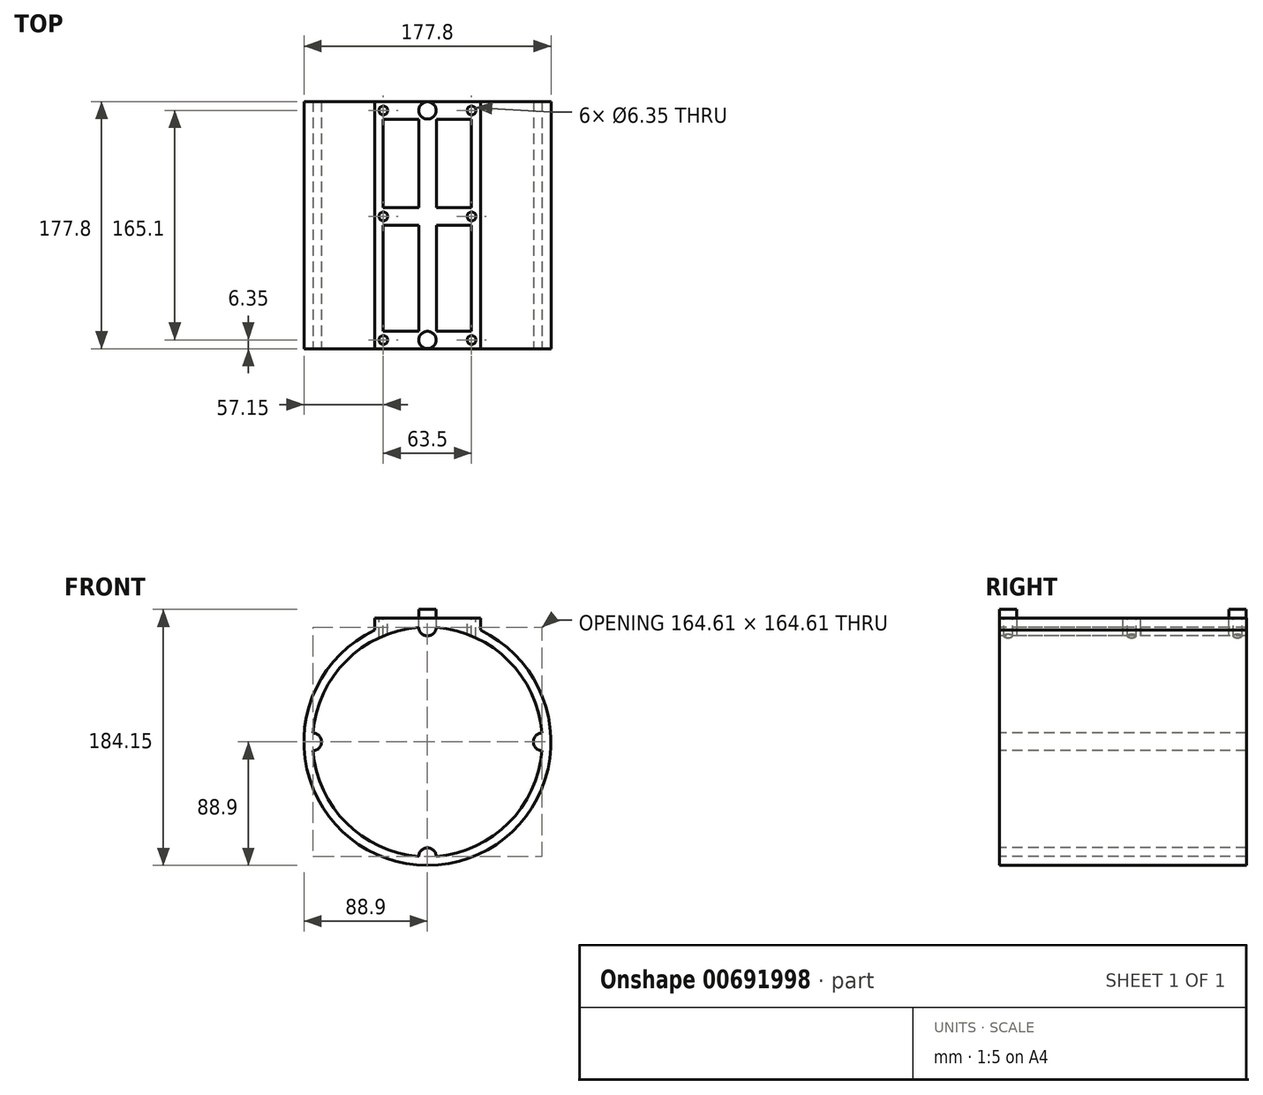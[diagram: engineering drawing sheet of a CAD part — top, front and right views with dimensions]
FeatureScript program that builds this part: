
annotation { "Feature Type Name" : "Feature", "Feature Type Description" : "" }
export const myFeature = defineFeature(function(context is Context, id is Id, definition is map)
    precondition{}
    {
        {
            var Q0;
            Q0=qCreatedBy(makeId("Front.planeOp"),FACE);
            var sketch = newSketch(context, id + "F0", { "sketchPlane" : qUnion([Q0])});
            skCircle(sketch, "E0", {"center": v(0, 0) * mm, "radius": 88.9 * mm});
            skLineSegment(sketch, "E1", {"start": v(0, 0) * mm, "end": v(0, 88.9) * mm});
            skLineSegment(sketch, "E2", {"start": v(0, 88.9) * mm, "end": v(38.1, 88.9) * mm});
            skLineSegment(sketch, "E3", {"start": v(38.1, 88.9) * mm, "end": v(-38.1, 88.9) * mm});
            skLineSegment(sketch, "E4", {"start": v(-38.1, 88.9) * mm, "end": v(-38.1, 80.32) * mm});
            skLineSegment(sketch, "E5", {"start": v(38.1, 88.9) * mm, "end": v(38.1, 80.32) * mm});
            skSolve(sketch);
        }
        {
            var Q0;
            Q0 = qSketchRegion(id + "F0", true);
            extrude(context, id + "F1", {"entities" : qUnion([Q0]), "oppositeDirection" : true, "depth" : 177.8 * mm, "offsetDistance" : 25.4 * mm});
        }
        {
            var Q0;
            Q0=makeQuery(id+"F1.opExtrude","CAP_FACE",FACE,{"disambiguationData":[OSD([sQuery(id+"F0.wireOp",EDGE,"E0"),sQuery(id+"F0.wireOp",EDGE,"E2"),sQuery(id+"F0.wireOp",EDGE,"E3"),sQuery(id+"F0.wireOp",EDGE,"E4"),sQuery(id+"F0.wireOp",EDGE,"E5")])],"isStart":true});
            var sketch = newSketch(context, id + "F2", { "sketchPlane" : qUnion([Q0])});
            skCircle(sketch, "E6", {"center": v(0, 0) * mm, "radius": 82.55 * mm});
            skSolve(sketch);
        }
        {
            var Q0;
            Q0=makeQuery(id+"F2.imprint","IMPRINT",FACE,{"disambiguationData":[TD([[makeQuery(id+"F2.imprint","IMPRINT",EDGE,{"derivedFrom":sQuery(id+"F2.wireOp",EDGE,"E6")}),1.0]])]});
            var sketch = newSketch(context, id + "F3", { "sketchPlane" : qUnion([Q0])});
            skLineSegment(sketch, "E7", {"start": v(0, 0) * mm, "end": v(0, 82.55) * mm});
            skLineSegment(sketch, "E8", {"start": v(0, 0) * mm, "end": v(82.55, 0) * mm});
            skLineSegment(sketch, "E9", {"start": v(0, 0) * mm, "end": v(-82.55, 0) * mm});
            skLineSegment(sketch, "E10", {"start": v(0, 0) * mm, "end": v(0, -82.55) * mm});
            skCircle(sketch, "E11", {"center": v(0, 82.55) * mm, "radius": 6.35 * mm});
            skCircle(sketch, "E12", {"center": v(82.55, 0) * mm, "radius": 6.35 * mm});
            skCircle(sketch, "E13", {"center": v(0, -82.55) * mm, "radius": 6.35 * mm});
            skCircle(sketch, "E14", {"center": v(-82.55, 0) * mm, "radius": 6.35 * mm});
            skSolve(sketch);
        }
        {
            var Q0;
            {var subQ5=sQuery(id+"F3.wireOp",EDGE,"E11");var subQ7=sQuery(id+"F3.wireOp",EDGE,"E7");var subQ8=makeQuery(id+"F3.imprint","INTERSECT",VERTEX,{"derivedFrom":[subQ7,subQ5]});Q0=makeQuery(id+"F3.imprint","IMPRINT",FACE,{"disambiguationData":[TD([[makeQuery(id+"F3.imprint","IMPRINT",EDGE,{"disambiguationData":[TD([[subQ8,1.0]])],"derivedFrom":subQ5}),-1.0]])]});}
            var Q1;
            {var subQ0=sQuery(id+"F3.wireOp",EDGE,"E13");var subQ1=sQuery(id+"F3.wireOp",EDGE,"E10");var subQ2=makeQuery(id+"F3.imprint","INTERSECT",VERTEX,{"derivedFrom":[subQ1,subQ0]});Q1=makeQuery(id+"F3.imprint","IMPRINT",FACE,{"disambiguationData":[TD([[makeQuery(id+"F3.imprint","IMPRINT",EDGE,{"disambiguationData":[TD([[subQ2,-1.0]])],"derivedFrom":subQ0}),-1.0]])]});}
            var Q2;
            {var subQ5=sQuery(id+"F3.wireOp",EDGE,"E7");var subQ7=sQuery(id+"F3.wireOp",EDGE,"E11");var subQ8=makeQuery(id+"F3.imprint","INTERSECT",VERTEX,{"derivedFrom":[subQ5,subQ7]});Q2=makeQuery(id+"F3.imprint","IMPRINT",FACE,{"disambiguationData":[TD([[makeQuery(id+"F3.imprint","IMPRINT",EDGE,{"disambiguationData":[TD([[subQ8,-1.0]])],"derivedFrom":subQ7}),-1.0]])]});}
            var Q3;
            {var subQ5=sQuery(id+"F3.wireOp",EDGE,"E8");var subQ7=sQuery(id+"F3.wireOp",EDGE,"E12");var subQ8=makeQuery(id+"F3.imprint","INTERSECT",VERTEX,{"derivedFrom":[subQ5,subQ7]});Q3=makeQuery(id+"F3.imprint","IMPRINT",FACE,{"disambiguationData":[TD([[makeQuery(id+"F3.imprint","IMPRINT",EDGE,{"disambiguationData":[TD([[subQ8,-1.0]])],"derivedFrom":subQ7}),-1.0]])]});}
            extrude(context, id + "F4", {"entities" : qUnion([Q0, Q1, Q2, Q3]), "operationType" : NewBodyOperationType.REMOVE, "endBound" : BoundingType.THROUGH_ALL, "oppositeDirection" : true, "depth" : 25.4 * mm, "offsetDistance" : 25.4 * mm});
        }
        {
            var Q0;
            Q0=makeQuery(id+"F1.opExtrude","SWEPT_FACE",FACE,{"disambiguationData":[OSD([sQuery(id+"F0.wireOp",EDGE,"E2"),sQuery(id+"F0.wireOp",EDGE,"E3")])]});
            var sketch = newSketch(context, id + "F5", { "sketchPlane" : qUnion([Q0])});
            skLineSegment(sketch, "E15", {"start": v(0, 0) * mm, "end": v(6.35, 0) * mm});
            skLineSegment(sketch, "E16", {"start": v(6.35, 0) * mm, "end": v(-6.35, 0) * mm});
            skLineSegment(sketch, "E17", {"start": v(-6.35, 0) * mm, "end": v(-6.35, 88.9) * mm});
            skLineSegment(sketch, "E18", {"start": v(-6.35, 177.8) * mm, "end": v(6.35, 177.8) * mm});
            skLineSegment(sketch, "E19", {"start": v(-6.35, 0) * mm, "end": v(-6.35, 12.7) * mm});
            skLineSegment(sketch, "E20", {"start": v(-6.35, 12.7) * mm, "end": v(-31.75, 12.7) * mm});
            skLineSegment(sketch, "E21", {"start": v(-31.75, 12.7) * mm, "end": v(-6.35, 12.7) * mm});
            skLineSegment(sketch, "E22", {"start": v(6.35, 12.7) * mm, "end": v(31.75, 12.7) * mm});
            skLineSegment(sketch, "E23", {"start": v(31.75, 12.7) * mm, "end": v(31.75, 177.8) * mm});
            skLineSegment(sketch, "E24", {"start": v(31.75, 177.8) * mm, "end": v(-31.75, 177.8) * mm});
            skLineSegment(sketch, "E25", {"start": v(-31.75, 177.8) * mm, "end": v(-31.75, 12.7) * mm});
            skLineSegment(sketch, "E26", {"start": v(-31.75, 177.8) * mm, "end": v(-31.75, 165.1) * mm});
            skLineSegment(sketch, "E27", {"start": v(-31.75, 165.1) * mm, "end": v(-6.35, 165.1) * mm});
            skLineSegment(sketch, "E28", {"start": v(31.75, 95.25) * mm, "end": v(31.75, 101.6) * mm});
            skLineSegment(sketch, "E29", {"start": v(31.75, 101.6) * mm, "end": v(6.35, 101.6) * mm});
            skLineSegment(sketch, "E30", {"start": v(-31.75, 101.6) * mm, "end": v(-31.75, 88.9) * mm});
            skLineSegment(sketch, "E31", {"start": v(-31.75, 88.9) * mm, "end": v(-6.35, 88.9) * mm});
            skLineSegment(sketch, "E32.trimOffspring", {"start": v(6.35, 165.1) * mm, "end": v(31.75, 165.1) * mm});
            skPoint(sketch, "E33.orphan", {"position": v(-31.75, 95.25) * mm});
            skLineSegment(sketch, "E34.trimOffspring", {"start": v(-6.35, 101.6) * mm, "end": v(-6.35, 165.1) * mm});
            skLineSegment(sketch, "E35.trimOffspring", {"start": v(6.35, 88.9) * mm, "end": v(6.35, 12.7) * mm});
            skLineSegment(sketch, "E36.trimOffspring", {"start": v(6.35, 88.9) * mm, "end": v(31.75, 88.9) * mm});
            skLineSegment(sketch, "E37", {"start": v(6.35, 165.1) * mm, "end": v(6.35, 101.6) * mm});
            skLineSegment(sketch, "E38.trimOffspring", {"start": v(-6.35, 101.6) * mm, "end": v(-31.75, 101.6) * mm});
            skSolve(sketch);
        }
        {
            var Q0;
            {var subQ1=sQuery(id+"F5.wireOp",EDGE,"E17");var subQ3=sQuery(id+"F5.wireOp",EDGE,"E31");var subQ4=makeQuery(id+"F5.imprint","INTERSECT",VERTEX,{"derivedFrom":[subQ1,subQ3]});Q0=makeQuery(id+"F5.imprint","IMPRINT",FACE,{"disambiguationData":[TD([[makeQuery(id+"F5.imprint","IMPRINT",EDGE,{"disambiguationData":[TD([[subQ4,1.0]])],"derivedFrom":subQ1}),1.0]])]});}
            var Q1;
            {var subQ0=sQuery(id+"F5.wireOp",EDGE,"E22");Q1=makeQuery(id+"F5.imprint","IMPRINT",FACE,{"disambiguationData":[TD([[makeQuery(id+"F5.imprint","IMPRINT",EDGE,{"derivedFrom":subQ0}),1.0]])]});}
            var Q2;
            {var subQ0=sQuery(id+"F5.wireOp",EDGE,"E29");var subQ1=sQuery(id+"F5.wireOp",EDGE,"E17");var subQ2=makeQuery(id+"F5.imprint","INTERSECT",VERTEX,{"derivedFrom":[subQ1,subQ0]});Q2=makeQuery(id+"F5.imprint","IMPRINT",FACE,{"disambiguationData":[TD([[makeQuery(id+"F5.imprint","IMPRINT",EDGE,{"disambiguationData":[TD([[subQ2,-1.0]])],"derivedFrom":subQ1}),1.0]])]});}
            var Q3;
            {var subQ0=sQuery(id+"F5.wireOp",EDGE,"E27");var subQ1=sQuery(id+"F5.wireOp",EDGE,"CNFkBtcS-LAWc-mXlH-B2Wr-kDQM0kjo4au6");var subQ2=makeQuery(id+"F5.imprint","INTERSECT",VERTEX,{"derivedFrom":[subQ1,subQ0]});Q3=makeQuery(id+"F5.imprint","IMPRINT",FACE,{"disambiguationData":[TD([[makeQuery(id+"F5.imprint","IMPRINT",EDGE,{"disambiguationData":[TD([[subQ2,-1.0]])],"derivedFrom":subQ1}),1.0]])]});}
            var Q4;
            {var subQ0=sQuery(id+"F5.wireOp",EDGE,"E29");Q4=makeQuery(id+"F5.imprint","IMPRINT",FACE,{"disambiguationData":[TD([[makeQuery(id+"F5.imprint","IMPRINT",EDGE,{"derivedFrom":subQ0}),-1.0]])]});}
            var Q5;
            {var subQ0=sQuery(id+"F5.wireOp",EDGE,"E27");Q5=makeQuery(id+"F5.imprint","IMPRINT",FACE,{"disambiguationData":[TD([[makeQuery(id+"F5.imprint","IMPRINT",EDGE,{"derivedFrom":subQ0}),-1.0]])]});}
            extrude(context, id + "F6", {"entities" : qUnion([Q0, Q1, Q2, Q3, Q4, Q5]), "operationType" : NewBodyOperationType.REMOVE, "oppositeDirection" : true, "depth" : 25.4 * mm, "offsetDistance" : 25.4 * mm});
        }
        {
            var Q0;
            Q0=makeQuery(id+"F1.opExtrude","SWEPT_FACE",FACE,{"disambiguationData":[OSD([sQuery(id+"F0.wireOp",EDGE,"E2"),sQuery(id+"F0.wireOp",EDGE,"E3")])]});
            var sketch = newSketch(context, id + "F7", { "sketchPlane" : qUnion([Q0])});
            skLineSegment(sketch, "E39", {"start": v(0, 0) * mm, "end": v(-31.75, 0) * mm});
            skCircle(sketch, "E40", {"center": v(-31.75, 171.45) * mm, "radius": 3.18 * mm});
            skCircle(sketch, "E41", {"center": v(31.75, 171.45) * mm, "radius": 3.18 * mm});
            skCircle(sketch, "E42", {"center": v(31.75, 95.25) * mm, "radius": 3.18 * mm});
            skCircle(sketch, "E43", {"center": v(-31.75, 95.25) * mm, "radius": 3.18 * mm});
            skCircle(sketch, "E44", {"center": v(-31.75, 6.35) * mm, "radius": 3.18 * mm});
            skCircle(sketch, "E45", {"center": v(31.75, 6.35) * mm, "radius": 3.18 * mm});
            skCircle(sketch, "E46", {"center": v(0, 171.45) * mm, "radius": 6.22 * mm});
            skPoint(sketch, "E47.center.orphan", {"position": v(0, 6.35) * mm});
            skCircle(sketch, "E48", {"center": v(0, 6.35) * mm, "radius": 6.22 * mm});
            skSolve(sketch);
        }
        {
            var Q0;
            Q0=makeQuery(id+"F7.imprint","IMPRINT",FACE,{"disambiguationData":[TD([[makeQuery(id+"F7.imprint","IMPRINT",EDGE,{"derivedFrom":sQuery(id+"F7.wireOp",EDGE,"E43")}),1.0]])]});
            var Q1;
            Q1=makeQuery(id+"F7.imprint","IMPRINT",FACE,{"disambiguationData":[TD([[makeQuery(id+"F7.imprint","IMPRINT",EDGE,{"derivedFrom":sQuery(id+"F7.wireOp",EDGE,"E40")}),1.0]])]});
            var Q2;
            Q2=makeQuery(id+"F7.imprint","IMPRINT",FACE,{"disambiguationData":[TD([[makeQuery(id+"F7.imprint","IMPRINT",EDGE,{"derivedFrom":sQuery(id+"F7.wireOp",EDGE,"E41")}),1.0]])]});
            var Q3;
            Q3=makeQuery(id+"F7.imprint","IMPRINT",FACE,{"disambiguationData":[TD([[makeQuery(id+"F7.imprint","IMPRINT",EDGE,{"derivedFrom":sQuery(id+"F7.wireOp",EDGE,"E42")}),1.0]])]});
            var Q4;
            Q4=makeQuery(id+"F7.imprint","IMPRINT",FACE,{"disambiguationData":[TD([[makeQuery(id+"F7.imprint","IMPRINT",EDGE,{"derivedFrom":sQuery(id+"F7.wireOp",EDGE,"E45")}),1.0]])]});
            var Q5;
            Q5=makeQuery(id+"F7.imprint","IMPRINT",FACE,{"disambiguationData":[TD([[makeQuery(id+"F7.imprint","IMPRINT",EDGE,{"derivedFrom":sQuery(id+"F7.wireOp",EDGE,"E44")}),1.0]])]});
            extrude(context, id + "F8", {"entities" : qUnion([Q0, Q1, Q2, Q3, Q4, Q5]), "operationType" : NewBodyOperationType.REMOVE, "oppositeDirection" : true, "depth" : 25.4 * mm, "offsetDistance" : 25.4 * mm});
        }
        {
            var Q0;
            Q0=makeQuery(id+"F7.imprint","IMPRINT",FACE,{"disambiguationData":[TD([[makeQuery(id+"F7.imprint","IMPRINT",EDGE,{"derivedFrom":sQuery(id+"F7.wireOp",EDGE,"E46")}),1.0]])]});
            var Q1;
            Q1=makeQuery(id+"F7.imprint","IMPRINT",FACE,{"disambiguationData":[TD([[makeQuery(id+"F7.imprint","IMPRINT",EDGE,{"derivedFrom":sQuery(id+"F7.wireOp",EDGE,"E47")}),1.0]])]});
            var Q2;
            Q2=makeQuery(id+"F7.imprint","IMPRINT",FACE,{"disambiguationData":[TD([[makeQuery(id+"F7.imprint","IMPRINT",EDGE,{"derivedFrom":sQuery(id+"F7.wireOp",EDGE,"E48")}),1.0]])]});
            extrude(context, id + "F9", {"entities" : qUnion([Q0, Q1, Q2]), "operationType" : NewBodyOperationType.ADD, "depth" : 6.35 * mm, "offsetDistance" : 25.4 * mm});
        }
    });
